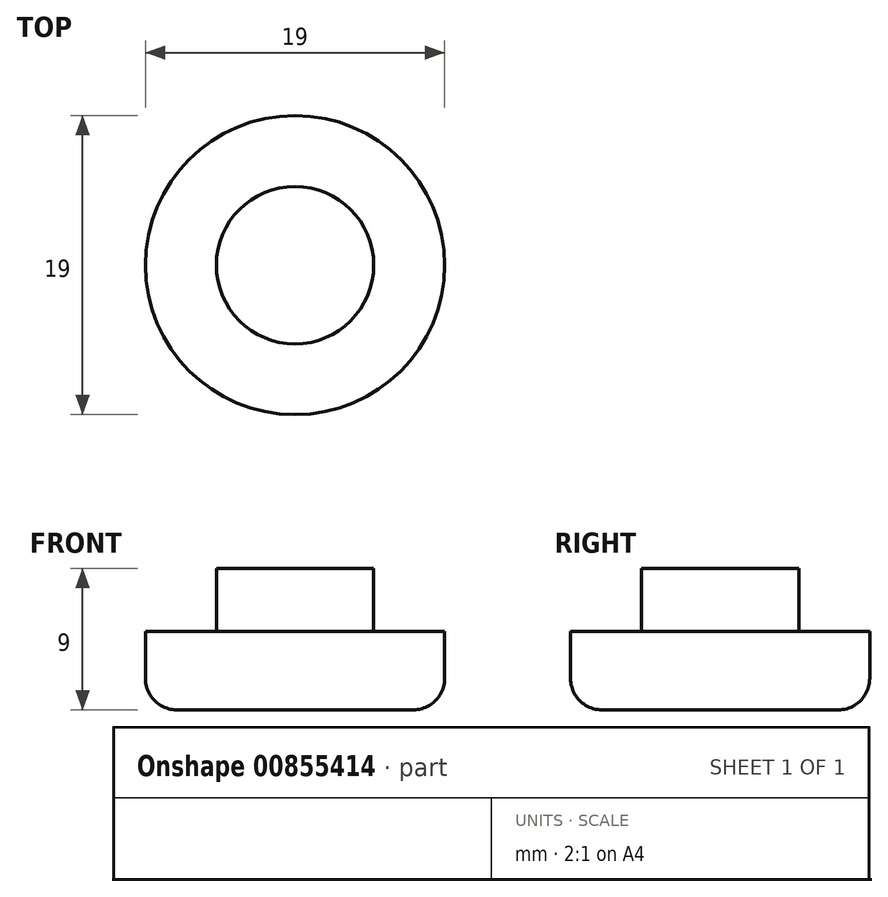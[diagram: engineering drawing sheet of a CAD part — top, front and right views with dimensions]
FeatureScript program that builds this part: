
annotation { "Feature Type Name" : "Feature", "Feature Type Description" : "" }
export const myFeature = defineFeature(function(context is Context, id is Id, definition is map)
    precondition{}
    {
        {
            var Q0;
            Q0=qCreatedBy(makeId("Top.planeOp"),FACE);
            var sketch = newSketch(context, id + "F0", { "sketchPlane" : qUnion([Q0])});
            skCircle(sketch, "E0", {"center": v(0, 0) * mm, "radius": 9.5 * mm});
            skSolve(sketch);
        }
        {
            var Q0;
            Q0=makeQuery(id+"F0.imprint","IMPRINT",FACE,{"disambiguationData":[TD([[makeQuery(id+"F0.imprint","IMPRINT",EDGE,{"derivedFrom":sQuery(id+"F0.wireOp",EDGE,"E0")}),1.0]])]});
            extrude(context, id + "F1", {"entities" : qUnion([Q0]), "depth" : 5 * mm, "offsetDistance" : 25 * mm});
        }
        {
            var Q0;
            Q0=qCreatedBy(makeId("Top.planeOp"),FACE);
            var sketch = newSketch(context, id + "F2", { "sketchPlane" : qUnion([Q0])});
            skCircle(sketch, "E1", {"center": v(0, 0) * mm, "radius": 5 * mm});
            skSolve(sketch);
        }
        {
            var Q0;
            Q0 = qSketchRegion(id + "F2", true);
            extrude(context, id + "F3", {"entities" : qUnion([Q0]), "operationType" : NewBodyOperationType.ADD, "depth" : 9 * mm, "offsetDistance" : 25 * mm});
        }
        {
            var Q0;
            Q0=makeQuery(id+"F1.opExtrude","CAP_EDGE",EDGE,{"disambiguationData":[OSD([sQuery(id+"F0.wireOp",EDGE,"E0")])],"isStart":true});
            fillet(context, id + "F4", {"entities" : qUnion([Q0]), "radius" : 2 * mm, "tangentPropagation" : true, "allowEdgeOverflow" : false});
        }
    });
